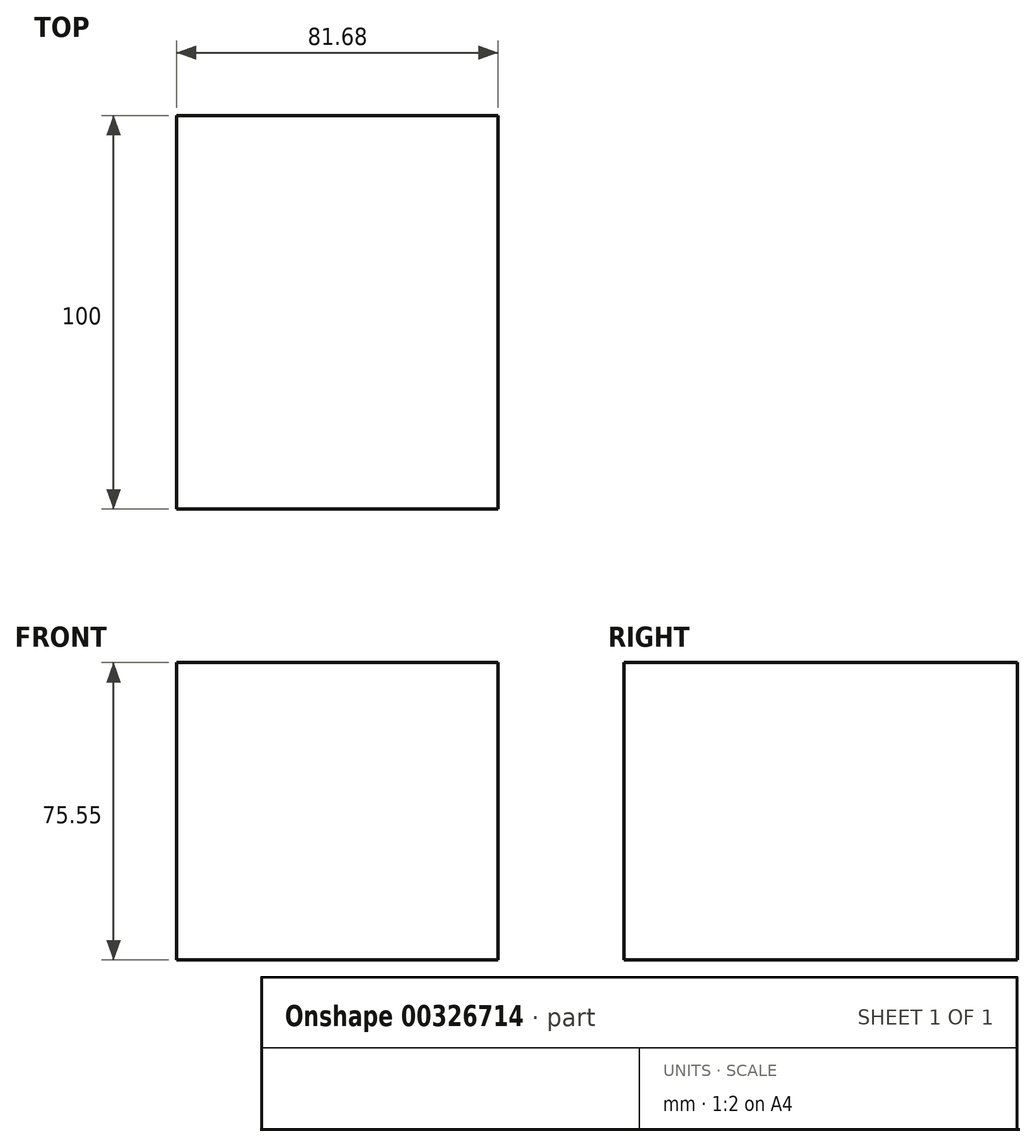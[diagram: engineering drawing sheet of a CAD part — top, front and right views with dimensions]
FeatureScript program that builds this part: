
annotation { "Feature Type Name" : "Feature", "Feature Type Description" : "" }
export const myFeature = defineFeature(function(context is Context, id is Id, definition is map)
    precondition{}
    {
        {
            var Q0;
            Q0=qCreatedBy(makeId("Front.planeOp"),FACE);
            var sketch = newSketch(context, id + "F0", { "sketchPlane" : qUnion([Q0])});
            skLineSegment(sketch, "E0.bottom", {"start": v(-37.37, -31.65) * mm, "end": v(44.3, -31.65) * mm});
            skLineSegment(sketch, "E0.top", {"start": v(-37.37, 43.9) * mm, "end": v(44.3, 43.9) * mm});
            skLineSegment(sketch, "E0.left", {"start": v(-37.37, -31.65) * mm, "end": v(-37.37, 43.9) * mm});
            skLineSegment(sketch, "E0.right", {"start": v(44.3, -31.65) * mm, "end": v(44.3, 43.9) * mm});
            skSolve(sketch);
        }
        {
            var Q0;
            Q0 = qSketchRegion(id + "F0", true);
            extrude(context, id + "F1", {"entities" : qUnion([Q0]), "depth" : 100 * mm});
        }
    });
